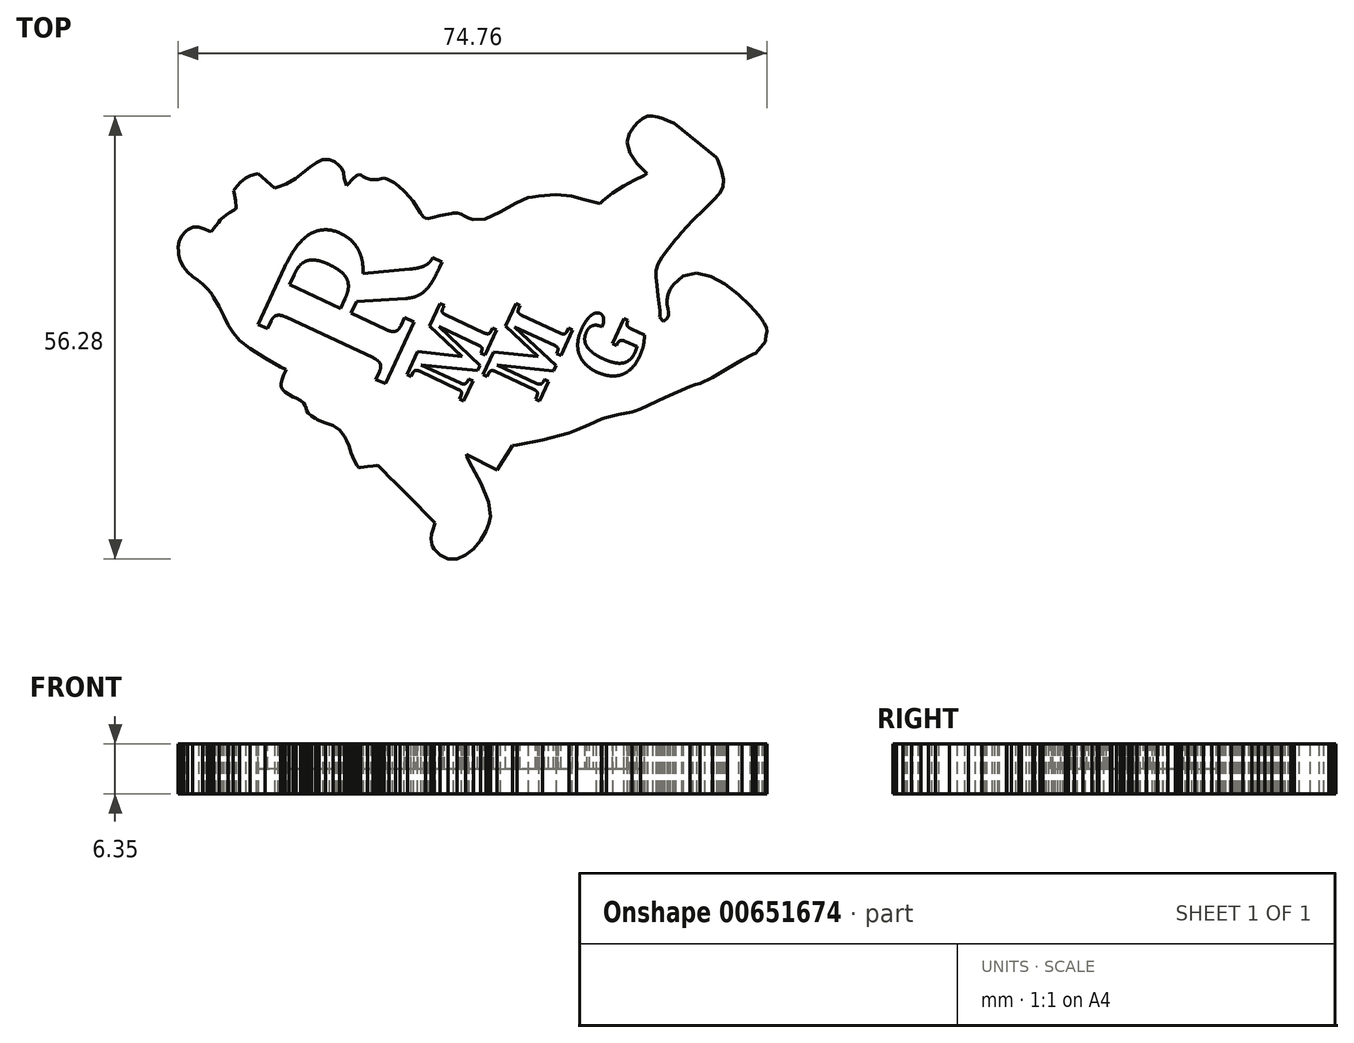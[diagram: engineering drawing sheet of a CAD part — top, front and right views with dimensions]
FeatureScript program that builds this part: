
annotation { "Feature Type Name" : "Feature", "Feature Type Description" : "" }
export const myFeature = defineFeature(function(context is Context, id is Id, definition is map)
    precondition{}
    {
        {
            var Q0;
            Q0=qCreatedBy(makeId("Top.planeOp"),FACE);
            var sketch = newSketch(context, id + "F0", { "sketchPlane" : qUnion([Q0])});
            skLineSegment(sketch, "E0", {"start": v(36, -1.99) * mm, "end": v(37.2, -0.53) * mm});
            skLineSegment(sketch, "E1", {"start": v(37.2, -0.53) * mm, "end": v(37.2, -0.33) * mm});
            skLineSegment(sketch, "E2", {"start": v(37.2, -0.33) * mm, "end": v(37.29, 0.26) * mm});
            skLineSegment(sketch, "E3", {"start": v(37.29, 0.26) * mm, "end": v(37.38, 0.75) * mm});
            skLineSegment(sketch, "E4", {"start": v(37.38, 0.75) * mm, "end": v(37.3, 1.24) * mm});
            skLineSegment(sketch, "E5", {"start": v(37.3, 1.24) * mm, "end": v(37, 1.85) * mm});
            skLineSegment(sketch, "E6", {"start": v(37, 1.85) * mm, "end": v(36.9, 2.04) * mm});
            skLineSegment(sketch, "E7", {"start": v(36.9, 2.04) * mm, "end": v(36.76, 2.25) * mm});
            skLineSegment(sketch, "E8", {"start": v(36.76, 2.25) * mm, "end": v(36.3, 2.84) * mm});
            skLineSegment(sketch, "E9", {"start": v(36.3, 2.84) * mm, "end": v(35.23, 4.06) * mm});
            skLineSegment(sketch, "E10", {"start": v(35.23, 4.06) * mm, "end": v(33.79, 5.46) * mm});
            skLineSegment(sketch, "E11", {"start": v(33.79, 5.46) * mm, "end": v(32.1, 6.77) * mm});
            skLineSegment(sketch, "E12", {"start": v(32.1, 6.77) * mm, "end": v(30.27, 7.76) * mm});
            skLineSegment(sketch, "E13", {"start": v(30.27, 7.76) * mm, "end": v(28.44, 8.18) * mm});
            skLineSegment(sketch, "E14", {"start": v(28.44, 8.18) * mm, "end": v(26.72, 7.78) * mm});
            skLineSegment(sketch, "E15", {"start": v(26.72, 7.78) * mm, "end": v(25.5, 6.74) * mm});
            skLineSegment(sketch, "E16", {"start": v(25.5, 6.74) * mm, "end": v(25.23, 6.3) * mm});
            skLineSegment(sketch, "E17", {"start": v(25.23, 6.3) * mm, "end": v(25.1, 6.12) * mm});
            skLineSegment(sketch, "E18", {"start": v(25.1, 6.12) * mm, "end": v(24.82, 5.48) * mm});
            skLineSegment(sketch, "E19", {"start": v(24.82, 5.48) * mm, "end": v(24.68, 4.78) * mm});
            skLineSegment(sketch, "E20", {"start": v(24.68, 4.78) * mm, "end": v(24.7, 4.17) * mm});
            skLineSegment(sketch, "E21", {"start": v(24.7, 4.17) * mm, "end": v(24.8, 3.65) * mm});
            skLineSegment(sketch, "E22", {"start": v(24.8, 3.65) * mm, "end": v(24.9, 3.2) * mm});
            skLineSegment(sketch, "E23", {"start": v(24.9, 3.2) * mm, "end": v(24.9, 2.8) * mm});
            skLineSegment(sketch, "E24", {"start": v(24.9, 2.8) * mm, "end": v(24.7, 2.42) * mm});
            skLineSegment(sketch, "E25", {"start": v(24.7, 2.42) * mm, "end": v(24.35, 2.14) * mm});
            skLineSegment(sketch, "E26", {"start": v(24.35, 2.14) * mm, "end": v(24.22, 2.07) * mm});
            skLineSegment(sketch, "E27", {"start": v(24.22, 2.07) * mm, "end": v(24.13, 2.18) * mm});
            skLineSegment(sketch, "E28", {"start": v(24.13, 2.18) * mm, "end": v(23.84, 2.5) * mm});
            skLineSegment(sketch, "E29", {"start": v(23.84, 2.5) * mm, "end": v(23.75, 2.6) * mm});
            skLineSegment(sketch, "E30", {"start": v(23.75, 2.6) * mm, "end": v(23.8, 2.8) * mm});
            skLineSegment(sketch, "E31", {"start": v(23.8, 2.8) * mm, "end": v(23.8, 3.28) * mm});
            skLineSegment(sketch, "E32", {"start": v(23.8, 3.28) * mm, "end": v(23.8, 3.44) * mm});
            skLineSegment(sketch, "E33", {"start": v(23.8, 3.44) * mm, "end": v(23.75, 3.9) * mm});
            skLineSegment(sketch, "E34", {"start": v(23.75, 3.9) * mm, "end": v(23.58, 5.26) * mm});
            skLineSegment(sketch, "E35", {"start": v(23.58, 5.26) * mm, "end": v(23.4, 6.62) * mm});
            skLineSegment(sketch, "E36", {"start": v(23.4, 6.62) * mm, "end": v(23.28, 7.67) * mm});
            skLineSegment(sketch, "E37", {"start": v(23.28, 7.67) * mm, "end": v(23.31, 8.52) * mm});
            skLineSegment(sketch, "E38", {"start": v(23.31, 8.52) * mm, "end": v(23.55, 9.33) * mm});
            skLineSegment(sketch, "E39", {"start": v(23.55, 9.33) * mm, "end": v(24.04, 10.22) * mm});
            skLineSegment(sketch, "E40", {"start": v(24.04, 10.22) * mm, "end": v(24.86, 11.32) * mm});
            skLineSegment(sketch, "E41", {"start": v(24.86, 11.32) * mm, "end": v(25.77, 12.41) * mm});
            skLineSegment(sketch, "E42", {"start": v(25.77, 12.41) * mm, "end": v(26.07, 12.77) * mm});
            skLineSegment(sketch, "E43", {"start": v(26.07, 12.77) * mm, "end": v(26.53, 13.3) * mm});
            skLineSegment(sketch, "E44", {"start": v(26.53, 13.3) * mm, "end": v(27.95, 14.84) * mm});
            skLineSegment(sketch, "E45", {"start": v(27.95, 14.84) * mm, "end": v(29.45, 16.34) * mm});
            skLineSegment(sketch, "E46", {"start": v(29.45, 16.34) * mm, "end": v(30.6, 17.44) * mm});
            skLineSegment(sketch, "E47", {"start": v(30.6, 17.44) * mm, "end": v(31.39, 18.31) * mm});
            skLineSegment(sketch, "E48", {"start": v(31.39, 18.31) * mm, "end": v(31.82, 19.12) * mm});
            skLineSegment(sketch, "E49", {"start": v(31.82, 19.12) * mm, "end": v(31.9, 20.03) * mm});
            skLineSegment(sketch, "E50", {"start": v(31.9, 20.03) * mm, "end": v(31.62, 21.22) * mm});
            skLineSegment(sketch, "E51", {"start": v(31.62, 21.22) * mm, "end": v(31.16, 22.44) * mm});
            skLineSegment(sketch, "E52", {"start": v(31.16, 22.44) * mm, "end": v(30.99, 22.84) * mm});
            skLineSegment(sketch, "E53", {"start": v(30.99, 22.84) * mm, "end": v(25.6, 27.24) * mm});
            skLineSegment(sketch, "E54", {"start": v(25.6, 27.24) * mm, "end": v(25.42, 27.3) * mm});
            skLineSegment(sketch, "E55", {"start": v(25.42, 27.3) * mm, "end": v(24.88, 27.5) * mm});
            skLineSegment(sketch, "E56", {"start": v(24.88, 27.5) * mm, "end": v(24.2, 27.79) * mm});
            skLineSegment(sketch, "E57", {"start": v(24.2, 27.79) * mm, "end": v(23.53, 28.02) * mm});
            skLineSegment(sketch, "E58", {"start": v(23.53, 28.02) * mm, "end": v(22.88, 28.14) * mm});
            skLineSegment(sketch, "E59", {"start": v(22.88, 28.14) * mm, "end": v(22.23, 28.1) * mm});
            skLineSegment(sketch, "E60", {"start": v(22.23, 28.1) * mm, "end": v(21.57, 27.81) * mm});
            skLineSegment(sketch, "E61", {"start": v(21.57, 27.81) * mm, "end": v(20.89, 27.24) * mm});
            skLineSegment(sketch, "E62", {"start": v(20.89, 27.24) * mm, "end": v(20.33, 26.55) * mm});
            skLineSegment(sketch, "E63", {"start": v(20.33, 26.55) * mm, "end": v(20.17, 26.3) * mm});
            skLineSegment(sketch, "E64", {"start": v(20.17, 26.3) * mm, "end": v(19.96, 25.98) * mm});
            skLineSegment(sketch, "E65", {"start": v(19.96, 25.98) * mm, "end": v(19.65, 24.8) * mm});
            skLineSegment(sketch, "E66", {"start": v(19.65, 24.8) * mm, "end": v(19.97, 23.43) * mm});
            skLineSegment(sketch, "E67", {"start": v(19.97, 23.43) * mm, "end": v(20.89, 22.11) * mm});
            skLineSegment(sketch, "E68", {"start": v(20.89, 22.11) * mm, "end": v(21.84, 21.12) * mm});
            skLineSegment(sketch, "E69", {"start": v(21.84, 21.12) * mm, "end": v(22.18, 20.8) * mm});
            skLineSegment(sketch, "E70", {"start": v(22.18, 20.8) * mm, "end": v(21.78, 20.59) * mm});
            skLineSegment(sketch, "E71", {"start": v(21.78, 20.59) * mm, "end": v(20.56, 19.98) * mm});
            skLineSegment(sketch, "E72", {"start": v(20.56, 19.98) * mm, "end": v(19.14, 19.26) * mm});
            skLineSegment(sketch, "E73", {"start": v(19.14, 19.26) * mm, "end": v(17.75, 18.35) * mm});
            skLineSegment(sketch, "E74", {"start": v(17.75, 18.35) * mm, "end": v(16.58, 17.37) * mm});
            skLineSegment(sketch, "E75", {"start": v(16.58, 17.37) * mm, "end": v(16.22, 17.02) * mm});
            skLineSegment(sketch, "E76", {"start": v(16.22, 17.02) * mm, "end": v(15.7, 17.11) * mm});
            skLineSegment(sketch, "E77", {"start": v(15.7, 17.11) * mm, "end": v(14.18, 17.51) * mm});
            skLineSegment(sketch, "E78", {"start": v(14.18, 17.51) * mm, "end": v(12.57, 17.95) * mm});
            skLineSegment(sketch, "E79", {"start": v(12.57, 17.95) * mm, "end": v(10.63, 18.13) * mm});
            skLineSegment(sketch, "E80", {"start": v(10.63, 18.13) * mm, "end": v(8.36, 17.97) * mm});
            skLineSegment(sketch, "E81", {"start": v(8.36, 17.97) * mm, "end": v(7.62, 17.86) * mm});
            skLineSegment(sketch, "E82", {"start": v(7.62, 17.86) * mm, "end": v(7.07, 17.77) * mm});
            skLineSegment(sketch, "E83", {"start": v(7.07, 17.77) * mm, "end": v(5.49, 17.1) * mm});
            skLineSegment(sketch, "E84", {"start": v(5.49, 17.1) * mm, "end": v(3.52, 15.94) * mm});
            skLineSegment(sketch, "E85", {"start": v(3.52, 15.94) * mm, "end": v(1.6, 15.06) * mm});
            skLineSegment(sketch, "E86", {"start": v(1.6, 15.06) * mm, "end": v(0.08, 14.95) * mm});
            skLineSegment(sketch, "E87", {"start": v(0.08, 14.95) * mm, "end": v(-0.35, 15.1) * mm});
            skLineSegment(sketch, "E88", {"start": v(-0.35, 15.1) * mm, "end": v(-0.53, 15.17) * mm});
            skLineSegment(sketch, "E89", {"start": v(-0.53, 15.17) * mm, "end": v(-1.03, 15.43) * mm});
            skLineSegment(sketch, "E90", {"start": v(-1.03, 15.43) * mm, "end": v(-1.44, 15.68) * mm});
            skLineSegment(sketch, "E91", {"start": v(-1.44, 15.68) * mm, "end": v(-1.9, 15.81) * mm});
            skLineSegment(sketch, "E92", {"start": v(-1.9, 15.81) * mm, "end": v(-2.48, 15.78) * mm});
            skLineSegment(sketch, "E93", {"start": v(-2.48, 15.78) * mm, "end": v(-2.67, 15.75) * mm});
            skLineSegment(sketch, "E94", {"start": v(-2.67, 15.75) * mm, "end": v(-3.03, 15.68) * mm});
            skLineSegment(sketch, "E95", {"start": v(-3.03, 15.68) * mm, "end": v(-4.11, 15.47) * mm});
            skLineSegment(sketch, "E96", {"start": v(-4.11, 15.47) * mm, "end": v(-5.07, 15.25) * mm});
            skLineSegment(sketch, "E97", {"start": v(-5.07, 15.25) * mm, "end": v(-5.67, 15.14) * mm});
            skLineSegment(sketch, "E98", {"start": v(-5.67, 15.14) * mm, "end": v(-6.05, 15.17) * mm});
            skLineSegment(sketch, "E99", {"start": v(-6.05, 15.17) * mm, "end": v(-6.32, 15.38) * mm});
            skLineSegment(sketch, "E100", {"start": v(-6.32, 15.38) * mm, "end": v(-6.61, 15.82) * mm});
            skLineSegment(sketch, "E101", {"start": v(-6.61, 15.82) * mm, "end": v(-7.05, 16.53) * mm});
            skLineSegment(sketch, "E102", {"start": v(-7.05, 16.53) * mm, "end": v(-7.56, 17.3) * mm});
            skLineSegment(sketch, "E103", {"start": v(-7.56, 17.3) * mm, "end": v(-7.75, 17.54) * mm});
            skLineSegment(sketch, "E104", {"start": v(-7.75, 17.54) * mm, "end": v(-7.87, 17.7) * mm});
            skLineSegment(sketch, "E105", {"start": v(-7.87, 17.7) * mm, "end": v(-8.74, 18.65) * mm});
            skLineSegment(sketch, "E106", {"start": v(-8.74, 18.65) * mm, "end": v(-9.8, 19.52) * mm});
            skLineSegment(sketch, "E107", {"start": v(-9.8, 19.52) * mm, "end": v(-10, 19.65) * mm});
            skLineSegment(sketch, "E108", {"start": v(-10, 19.65) * mm, "end": v(-10.2, 19.78) * mm});
            skLineSegment(sketch, "E109", {"start": v(-10.2, 19.78) * mm, "end": v(-10.84, 20.13) * mm});
            skLineSegment(sketch, "E110", {"start": v(-10.84, 20.13) * mm, "end": v(-11.25, 20.24) * mm});
            skLineSegment(sketch, "E111", {"start": v(-11.25, 20.24) * mm, "end": v(-11.57, 20.16) * mm});
            skLineSegment(sketch, "E112", {"start": v(-11.57, 20.16) * mm, "end": v(-11.98, 20.06) * mm});
            skLineSegment(sketch, "E113", {"start": v(-11.98, 20.06) * mm, "end": v(-12.12, 20.05) * mm});
            skLineSegment(sketch, "E114", {"start": v(-12.12, 20.05) * mm, "end": v(-12.33, 20.04) * mm});
            skLineSegment(sketch, "E115", {"start": v(-12.33, 20.04) * mm, "end": v(-12.96, 20.07) * mm});
            skLineSegment(sketch, "E116", {"start": v(-12.96, 20.07) * mm, "end": v(-13.51, 20.24) * mm});
            skLineSegment(sketch, "E117", {"start": v(-13.51, 20.24) * mm, "end": v(-13.88, 20.47) * mm});
            skLineSegment(sketch, "E118", {"start": v(-13.88, 20.47) * mm, "end": v(-14.15, 20.66) * mm});
            skLineSegment(sketch, "E119", {"start": v(-14.15, 20.66) * mm, "end": v(-14.41, 20.72) * mm});
            skLineSegment(sketch, "E120", {"start": v(-14.41, 20.72) * mm, "end": v(-14.74, 20.58) * mm});
            skLineSegment(sketch, "E121", {"start": v(-14.74, 20.58) * mm, "end": v(-15.24, 20.13) * mm});
            skLineSegment(sketch, "E122", {"start": v(-15.24, 20.13) * mm, "end": v(-15.8, 19.5) * mm});
            skLineSegment(sketch, "E123", {"start": v(-15.8, 19.5) * mm, "end": v(-15.99, 19.29) * mm});
            skLineSegment(sketch, "E124", {"start": v(-15.99, 19.29) * mm, "end": v(-16.1, 19.5) * mm});
            skLineSegment(sketch, "E125", {"start": v(-16.1, 19.5) * mm, "end": v(-16.3, 20.22) * mm});
            skLineSegment(sketch, "E126", {"start": v(-16.3, 20.22) * mm, "end": v(-16.4, 20.93) * mm});
            skLineSegment(sketch, "E127", {"start": v(-16.4, 20.93) * mm, "end": v(-16.64, 21.53) * mm});
            skLineSegment(sketch, "E128", {"start": v(-16.64, 21.53) * mm, "end": v(-17.15, 22.05) * mm});
            skLineSegment(sketch, "E129", {"start": v(-17.15, 22.05) * mm, "end": v(-17.34, 22.18) * mm});
            skLineSegment(sketch, "E130", {"start": v(-17.34, 22.18) * mm, "end": v(-17.55, 22.32) * mm});
            skLineSegment(sketch, "E131", {"start": v(-17.55, 22.32) * mm, "end": v(-18.25, 22.6) * mm});
            skLineSegment(sketch, "E132", {"start": v(-18.25, 22.6) * mm, "end": v(-19.07, 22.57) * mm});
            skLineSegment(sketch, "E133", {"start": v(-19.07, 22.57) * mm, "end": v(-19.85, 22.22) * mm});
            skLineSegment(sketch, "E134", {"start": v(-19.85, 22.22) * mm, "end": v(-20.64, 21.63) * mm});
            skLineSegment(sketch, "E135", {"start": v(-20.64, 21.63) * mm, "end": v(-21.5, 20.92) * mm});
            skLineSegment(sketch, "E136", {"start": v(-21.5, 20.92) * mm, "end": v(-22.5, 20.17) * mm});
            skLineSegment(sketch, "E137", {"start": v(-22.5, 20.17) * mm, "end": v(-23.7, 19.5) * mm});
            skLineSegment(sketch, "E138", {"start": v(-23.7, 19.5) * mm, "end": v(-24.78, 19.1) * mm});
            skLineSegment(sketch, "E139", {"start": v(-24.78, 19.1) * mm, "end": v(-25.15, 19) * mm});
            skLineSegment(sketch, "E140", {"start": v(-25.15, 19) * mm, "end": v(-27.25, 20.81) * mm});
            skLineSegment(sketch, "E141", {"start": v(-27.25, 20.81) * mm, "end": v(-27.48, 20.75) * mm});
            skLineSegment(sketch, "E142", {"start": v(-27.48, 20.75) * mm, "end": v(-28.18, 20.56) * mm});
            skLineSegment(sketch, "E143", {"start": v(-28.18, 20.56) * mm, "end": v(-28.85, 20.24) * mm});
            skLineSegment(sketch, "E144", {"start": v(-28.85, 20.24) * mm, "end": v(-29.5, 19.67) * mm});
            skLineSegment(sketch, "E145", {"start": v(-29.5, 19.67) * mm, "end": v(-30.17, 18.9) * mm});
            skLineSegment(sketch, "E146", {"start": v(-30.17, 18.9) * mm, "end": v(-30.38, 18.64) * mm});
            skLineSegment(sketch, "E147", {"start": v(-30.38, 18.64) * mm, "end": v(-30.32, 18.41) * mm});
            skLineSegment(sketch, "E148", {"start": v(-30.32, 18.41) * mm, "end": v(-30.1, 17.38) * mm});
            skLineSegment(sketch, "E149", {"start": v(-30.1, 17.38) * mm, "end": v(-30.06, 16.48) * mm});
            skLineSegment(sketch, "E150", {"start": v(-30.06, 16.48) * mm, "end": v(-30.09, 16.33) * mm});
            skLineSegment(sketch, "E151", {"start": v(-30.09, 16.33) * mm, "end": v(-30.27, 16.21) * mm});
            skLineSegment(sketch, "E152", {"start": v(-30.27, 16.21) * mm, "end": v(-30.83, 15.86) * mm});
            skLineSegment(sketch, "E153", {"start": v(-30.83, 15.86) * mm, "end": v(-31.33, 15.55) * mm});
            skLineSegment(sketch, "E154", {"start": v(-31.33, 15.55) * mm, "end": v(-31.64, 15.32) * mm});
            skLineSegment(sketch, "E155", {"start": v(-31.64, 15.32) * mm, "end": v(-31.85, 15.13) * mm});
            skLineSegment(sketch, "E156", {"start": v(-31.85, 15.13) * mm, "end": v(-32.04, 14.9) * mm});
            skLineSegment(sketch, "E157", {"start": v(-32.04, 14.9) * mm, "end": v(-32.28, 14.59) * mm});
            skLineSegment(sketch, "E158", {"start": v(-32.28, 14.59) * mm, "end": v(-32.66, 14.12) * mm});
            skLineSegment(sketch, "E159", {"start": v(-32.66, 14.12) * mm, "end": v(-33.09, 13.61) * mm});
            skLineSegment(sketch, "E160", {"start": v(-33.09, 13.61) * mm, "end": v(-33.23, 13.44) * mm});
            skLineSegment(sketch, "E161", {"start": v(-33.23, 13.44) * mm, "end": v(-33.45, 13.52) * mm});
            skLineSegment(sketch, "E162", {"start": v(-33.45, 13.52) * mm, "end": v(-34.07, 13.78) * mm});
            skLineSegment(sketch, "E163", {"start": v(-34.07, 13.78) * mm, "end": v(-34.79, 14.03) * mm});
            skLineSegment(sketch, "E164", {"start": v(-34.79, 14.03) * mm, "end": v(-35.5, 14.03) * mm});
            skLineSegment(sketch, "E165", {"start": v(-35.5, 14.03) * mm, "end": v(-36.13, 13.73) * mm});
            skLineSegment(sketch, "E166", {"start": v(-36.13, 13.73) * mm, "end": v(-36.3, 13.58) * mm});
            skLineSegment(sketch, "E167", {"start": v(-36.3, 13.58) * mm, "end": v(-36.49, 13.44) * mm});
            skLineSegment(sketch, "E168", {"start": v(-36.49, 13.44) * mm, "end": v(-36.94, 12.91) * mm});
            skLineSegment(sketch, "E169", {"start": v(-36.94, 12.91) * mm, "end": v(-37.27, 12.19) * mm});
            skLineSegment(sketch, "E170", {"start": v(-37.27, 12.19) * mm, "end": v(-37.38, 11.46) * mm});
            skLineSegment(sketch, "E171", {"start": v(-37.38, 11.46) * mm, "end": v(-37.37, 10.94) * mm});
            skLineSegment(sketch, "E172", {"start": v(-37.37, 10.94) * mm, "end": v(-37.35, 10.77) * mm});
            skLineSegment(sketch, "E173", {"start": v(-37.35, 10.77) * mm, "end": v(-37.32, 10.52) * mm});
            skLineSegment(sketch, "E174", {"start": v(-37.32, 10.52) * mm, "end": v(-37.13, 9.76) * mm});
            skLineSegment(sketch, "E175", {"start": v(-37.13, 9.76) * mm, "end": v(-36.73, 8.96) * mm});
            skLineSegment(sketch, "E176", {"start": v(-36.73, 8.96) * mm, "end": v(-36.21, 8.31) * mm});
            skLineSegment(sketch, "E177", {"start": v(-36.21, 8.31) * mm, "end": v(-35.6, 7.77) * mm});
            skLineSegment(sketch, "E178", {"start": v(-35.6, 7.77) * mm, "end": v(-34.94, 7.27) * mm});
            skLineSegment(sketch, "E179", {"start": v(-34.94, 7.27) * mm, "end": v(-34.28, 6.76) * mm});
            skLineSegment(sketch, "E180", {"start": v(-34.28, 6.76) * mm, "end": v(-33.65, 6.18) * mm});
            skLineSegment(sketch, "E181", {"start": v(-33.65, 6.18) * mm, "end": v(-33.23, 5.67) * mm});
            skLineSegment(sketch, "E182", {"start": v(-33.23, 5.67) * mm, "end": v(-33.1, 5.48) * mm});
            skLineSegment(sketch, "E183", {"start": v(-33.1, 5.48) * mm, "end": v(-32.87, 5.1) * mm});
            skLineSegment(sketch, "E184", {"start": v(-32.87, 5.1) * mm, "end": v(-32.22, 3.93) * mm});
            skLineSegment(sketch, "E185", {"start": v(-32.22, 3.93) * mm, "end": v(-31.6, 2.66) * mm});
            skLineSegment(sketch, "E186", {"start": v(-31.6, 2.66) * mm, "end": v(-31.06, 1.58) * mm});
            skLineSegment(sketch, "E187", {"start": v(-31.06, 1.58) * mm, "end": v(-30.44, 0.6) * mm});
            skLineSegment(sketch, "E188", {"start": v(-30.44, 0.6) * mm, "end": v(-29.57, -0.36) * mm});
            skLineSegment(sketch, "E189", {"start": v(-29.57, -0.36) * mm, "end": v(-28.27, -1.4) * mm});
            skLineSegment(sketch, "E190", {"start": v(-28.27, -1.4) * mm, "end": v(-26.37, -2.62) * mm});
            skLineSegment(sketch, "E191", {"start": v(-26.37, -2.62) * mm, "end": v(-24.37, -3.74) * mm});
            skLineSegment(sketch, "E192", {"start": v(-24.37, -3.74) * mm, "end": v(-23.7, -4.1) * mm});
            skLineSegment(sketch, "E193", {"start": v(-23.7, -4.1) * mm, "end": v(-23.77, -4.27) * mm});
            skLineSegment(sketch, "E194", {"start": v(-23.77, -4.27) * mm, "end": v(-23.99, -4.78) * mm});
            skLineSegment(sketch, "E195", {"start": v(-23.99, -4.78) * mm, "end": v(-24.2, -5.35) * mm});
            skLineSegment(sketch, "E196", {"start": v(-24.2, -5.35) * mm, "end": v(-24.32, -5.82) * mm});
            skLineSegment(sketch, "E197", {"start": v(-24.32, -5.82) * mm, "end": v(-24.32, -6.23) * mm});
            skLineSegment(sketch, "E198", {"start": v(-24.32, -6.23) * mm, "end": v(-24.16, -6.58) * mm});
            skLineSegment(sketch, "E199", {"start": v(-24.16, -6.58) * mm, "end": v(-23.84, -6.92) * mm});
            skLineSegment(sketch, "E200", {"start": v(-23.84, -6.92) * mm, "end": v(-23.33, -7.26) * mm});
            skLineSegment(sketch, "E201", {"start": v(-23.33, -7.26) * mm, "end": v(-22.78, -7.54) * mm});
            skLineSegment(sketch, "E202", {"start": v(-22.78, -7.54) * mm, "end": v(-22.6, -7.62) * mm});
            skLineSegment(sketch, "E203", {"start": v(-22.6, -7.62) * mm, "end": v(-22.41, -7.7) * mm});
            skLineSegment(sketch, "E204", {"start": v(-22.41, -7.7) * mm, "end": v(-21.87, -8) * mm});
            skLineSegment(sketch, "E205", {"start": v(-21.87, -8) * mm, "end": v(-21.46, -8.35) * mm});
            skLineSegment(sketch, "E206", {"start": v(-21.46, -8.35) * mm, "end": v(-21.25, -8.66) * mm});
            skLineSegment(sketch, "E207", {"start": v(-21.25, -8.66) * mm, "end": v(-21.16, -8.97) * mm});
            skLineSegment(sketch, "E208", {"start": v(-21.16, -8.97) * mm, "end": v(-21.06, -9.27) * mm});
            skLineSegment(sketch, "E209", {"start": v(-21.06, -9.27) * mm, "end": v(-20.87, -9.6) * mm});
            skLineSegment(sketch, "E210", {"start": v(-20.87, -9.6) * mm, "end": v(-20.48, -9.98) * mm});
            skLineSegment(sketch, "E211", {"start": v(-20.48, -9.98) * mm, "end": v(-19.96, -10.3) * mm});
            skLineSegment(sketch, "E212", {"start": v(-19.96, -10.3) * mm, "end": v(-19.78, -10.4) * mm});
            skLineSegment(sketch, "E213", {"start": v(-19.78, -10.4) * mm, "end": v(-19.52, -10.54) * mm});
            skLineSegment(sketch, "E214", {"start": v(-19.52, -10.54) * mm, "end": v(-18.68, -10.86) * mm});
            skLineSegment(sketch, "E215", {"start": v(-18.68, -10.86) * mm, "end": v(-17.73, -11.21) * mm});
            skLineSegment(sketch, "E216", {"start": v(-17.73, -11.21) * mm, "end": v(-16.88, -11.77) * mm});
            skLineSegment(sketch, "E217", {"start": v(-16.88, -11.77) * mm, "end": v(-16.26, -12.56) * mm});
            skLineSegment(sketch, "E218", {"start": v(-16.26, -12.56) * mm, "end": v(-16.1, -12.86) * mm});
            skLineSegment(sketch, "E219", {"start": v(-16.1, -12.86) * mm, "end": v(-15.99, -13.08) * mm});
            skLineSegment(sketch, "E220", {"start": v(-15.99, -13.08) * mm, "end": v(-15.7, -13.8) * mm});
            skLineSegment(sketch, "E221", {"start": v(-15.7, -13.8) * mm, "end": v(-15.42, -14.67) * mm});
            skLineSegment(sketch, "E222", {"start": v(-15.42, -14.67) * mm, "end": v(-15.07, -15.54) * mm});
            skLineSegment(sketch, "E223", {"start": v(-15.07, -15.54) * mm, "end": v(-14.65, -16.28) * mm});
            skLineSegment(sketch, "E224", {"start": v(-14.65, -16.28) * mm, "end": v(-14.49, -16.51) * mm});
            skLineSegment(sketch, "E225", {"start": v(-14.49, -16.51) * mm, "end": v(-14.2, -16.5) * mm});
            skLineSegment(sketch, "E226", {"start": v(-14.2, -16.5) * mm, "end": v(-13.36, -16.42) * mm});
            skLineSegment(sketch, "E227", {"start": v(-13.36, -16.42) * mm, "end": v(-12.65, -16.32) * mm});
            skLineSegment(sketch, "E228", {"start": v(-12.65, -16.32) * mm, "end": v(-12.22, -16.28) * mm});
            skLineSegment(sketch, "E229", {"start": v(-12.22, -16.28) * mm, "end": v(-11.94, -16.34) * mm});
            skLineSegment(sketch, "E230", {"start": v(-11.94, -16.34) * mm, "end": v(-11.66, -16.56) * mm});
            skLineSegment(sketch, "E231", {"start": v(-11.66, -16.56) * mm, "end": v(-11.26, -17) * mm});
            skLineSegment(sketch, "E232", {"start": v(-11.26, -17) * mm, "end": v(-10.6, -17.72) * mm});
            skLineSegment(sketch, "E233", {"start": v(-10.6, -17.72) * mm, "end": v(-9.8, -18.51) * mm});
            skLineSegment(sketch, "E234", {"start": v(-9.8, -18.51) * mm, "end": v(-9.52, -18.77) * mm});
            skLineSegment(sketch, "E235", {"start": v(-9.52, -18.77) * mm, "end": v(-9.2, -19.07) * mm});
            skLineSegment(sketch, "E236", {"start": v(-9.2, -19.07) * mm, "end": v(-8.25, -20) * mm});
            skLineSegment(sketch, "E237", {"start": v(-8.25, -20) * mm, "end": v(-7.1, -21.18) * mm});
            skLineSegment(sketch, "E238", {"start": v(-7.1, -21.18) * mm, "end": v(-5.98, -22.34) * mm});
            skLineSegment(sketch, "E239", {"start": v(-5.98, -22.34) * mm, "end": v(-5.07, -23.25) * mm});
            skLineSegment(sketch, "E240", {"start": v(-5.07, -23.25) * mm, "end": v(-4.76, -23.55) * mm});
            skLineSegment(sketch, "E241", {"start": v(-4.76, -23.55) * mm, "end": v(-4.8, -23.76) * mm});
            skLineSegment(sketch, "E242", {"start": v(-4.8, -23.76) * mm, "end": v(-5, -24.36) * mm});
            skLineSegment(sketch, "E243", {"start": v(-5, -24.36) * mm, "end": v(-5.2, -24.98) * mm});
            skLineSegment(sketch, "E244", {"start": v(-5.2, -24.98) * mm, "end": v(-5.26, -25.63) * mm});
            skLineSegment(sketch, "E245", {"start": v(-5.26, -25.63) * mm, "end": v(-5.16, -26.33) * mm});
            skLineSegment(sketch, "E246", {"start": v(-5.16, -26.33) * mm, "end": v(-5.1, -26.55) * mm});
            skLineSegment(sketch, "E247", {"start": v(-5.1, -26.55) * mm, "end": v(-4.92, -26.86) * mm});
            skLineSegment(sketch, "E248", {"start": v(-4.92, -26.86) * mm, "end": v(-4.15, -27.65) * mm});
            skLineSegment(sketch, "E249", {"start": v(-4.15, -27.65) * mm, "end": v(-3.1, -28.14) * mm});
            skLineSegment(sketch, "E250", {"start": v(-3.1, -28.14) * mm, "end": v(-1.99, -28.11) * mm});
            skLineSegment(sketch, "E251", {"start": v(-1.99, -28.11) * mm, "end": v(-0.9, -27.65) * mm});
            skLineSegment(sketch, "E252", {"start": v(-0.9, -27.65) * mm, "end": v(0.13, -26.85) * mm});
            skLineSegment(sketch, "E253", {"start": v(0.13, -26.85) * mm, "end": v(1.02, -25.8) * mm});
            skLineSegment(sketch, "E254", {"start": v(1.02, -25.8) * mm, "end": v(1.71, -24.57) * mm});
            skLineSegment(sketch, "E255", {"start": v(1.71, -24.57) * mm, "end": v(2.08, -23.6) * mm});
            skLineSegment(sketch, "E256", {"start": v(2.08, -23.6) * mm, "end": v(2.16, -23.26) * mm});
            skLineSegment(sketch, "E257", {"start": v(2.16, -23.26) * mm, "end": v(2.28, -22.72) * mm});
            skLineSegment(sketch, "E258", {"start": v(2.28, -22.72) * mm, "end": v(2.03, -20.93) * mm});
            skLineSegment(sketch, "E259", {"start": v(2.03, -20.93) * mm, "end": v(1.07, -18.56) * mm});
            skLineSegment(sketch, "E260", {"start": v(1.07, -18.56) * mm, "end": v(-0.07, -16.43) * mm});
            skLineSegment(sketch, "E261", {"start": v(-0.07, -16.43) * mm, "end": v(-0.68, -15.26) * mm});
            skLineSegment(sketch, "E262", {"start": v(-0.68, -15.26) * mm, "end": v(-0.76, -14.85) * mm});
            skLineSegment(sketch, "E263", {"start": v(-0.76, -14.85) * mm, "end": v(3.1, -16.84) * mm});
            skLineSegment(sketch, "E264", {"start": v(3.1, -16.84) * mm, "end": v(5.05, -13.71) * mm});
            skLineSegment(sketch, "E265", {"start": v(5.05, -13.71) * mm, "end": v(5.62, -13.66) * mm});
            skLineSegment(sketch, "E266", {"start": v(5.62, -13.66) * mm, "end": v(8.9, -13.05) * mm});
            skLineSegment(sketch, "E267", {"start": v(8.9, -13.05) * mm, "end": v(12.27, -12.12) * mm});
            skLineSegment(sketch, "E268", {"start": v(12.27, -12.12) * mm, "end": v(12.88, -11.9) * mm});
            skLineSegment(sketch, "E269", {"start": v(12.88, -11.9) * mm, "end": v(13.23, -11.79) * mm});
            skLineSegment(sketch, "E270", {"start": v(13.23, -11.79) * mm, "end": v(14.83, -11.08) * mm});
            skLineSegment(sketch, "E271", {"start": v(14.83, -11.08) * mm, "end": v(16.4, -10.37) * mm});
            skLineSegment(sketch, "E272", {"start": v(16.4, -10.37) * mm, "end": v(16.73, -10.24) * mm});
            skLineSegment(sketch, "E273", {"start": v(16.73, -10.24) * mm, "end": v(17.01, -10.14) * mm});
            skLineSegment(sketch, "E274", {"start": v(17.01, -10.14) * mm, "end": v(18.54, -9.81) * mm});
            skLineSegment(sketch, "E275", {"start": v(18.54, -9.81) * mm, "end": v(20.26, -9.44) * mm});
            skLineSegment(sketch, "E276", {"start": v(20.26, -9.44) * mm, "end": v(20.63, -9.31) * mm});
            skLineSegment(sketch, "E277", {"start": v(20.63, -9.31) * mm, "end": v(21.3, -9.08) * mm});
            skLineSegment(sketch, "E278", {"start": v(21.3, -9.08) * mm, "end": v(24.47, -7.65) * mm});
            skLineSegment(sketch, "E279", {"start": v(24.47, -7.65) * mm, "end": v(27.64, -6.23) * mm});
            skLineSegment(sketch, "E280", {"start": v(27.64, -6.23) * mm, "end": v(28.3, -6) * mm});
            skLineSegment(sketch, "E281", {"start": v(28.3, -6) * mm, "end": v(28.86, -5.82) * mm});
            skLineSegment(sketch, "E282", {"start": v(28.86, -5.82) * mm, "end": v(30.46, -5.08) * mm});
            skLineSegment(sketch, "E283", {"start": v(30.46, -5.08) * mm, "end": v(32.4, -3.97) * mm});
            skLineSegment(sketch, "E284", {"start": v(32.4, -3.97) * mm, "end": v(34.2, -2.87) * mm});
            skLineSegment(sketch, "E285", {"start": v(34.2, -2.87) * mm, "end": v(35.54, -2.17) * mm});
            skLineSegment(sketch, "E286", {"start": v(35.54, -2.17) * mm, "end": v(36, -1.99) * mm});
            skSolve(sketch);
        }
        {
            var Q0;
            Q0=makeQuery(id+"F0.imprint","IMPRINT",FACE,{"disambiguationData":[TD([[makeQuery(id+"F0.imprint","IMPRINT",EDGE,{"derivedFrom":sQuery(id+"F0.wireOp",EDGE,"E0")}),1.0]])]});
            extrude(context, id + "F1", {"entities" : qUnion([Q0]), "depth" : 6.35 * mm, "offsetDistance" : 25.4 * mm});
        }
        {
            var Q0;
            Q0=makeQuery(id+"F1.opExtrude","CAP_FACE",FACE,{"disambiguationData":[OSD([sQuery(id+"F0.wireOp",EDGE,"E0"),sQuery(id+"F0.wireOp",EDGE,"E1"),sQuery(id+"F0.wireOp",EDGE,"E2"),sQuery(id+"F0.wireOp",EDGE,"E3"),sQuery(id+"F0.wireOp",EDGE,"E4"),sQuery(id+"F0.wireOp",EDGE,"E5"),sQuery(id+"F0.wireOp",EDGE,"E6"),sQuery(id+"F0.wireOp",EDGE,"E7"),sQuery(id+"F0.wireOp",EDGE,"E8"),sQuery(id+"F0.wireOp",EDGE,"E9"),sQuery(id+"F0.wireOp",EDGE,"E10"),sQuery(id+"F0.wireOp",EDGE,"E11"),sQuery(id+"F0.wireOp",EDGE,"E12"),sQuery(id+"F0.wireOp",EDGE,"E13"),sQuery(id+"F0.wireOp",EDGE,"E14"),sQuery(id+"F0.wireOp",EDGE,"E15"),sQuery(id+"F0.wireOp",EDGE,"E16"),sQuery(id+"F0.wireOp",EDGE,"E17"),sQuery(id+"F0.wireOp",EDGE,"E18"),sQuery(id+"F0.wireOp",EDGE,"E19"),sQuery(id+"F0.wireOp",EDGE,"E20"),sQuery(id+"F0.wireOp",EDGE,"E21"),sQuery(id+"F0.wireOp",EDGE,"E22"),sQuery(id+"F0.wireOp",EDGE,"E23"),sQuery(id+"F0.wireOp",EDGE,"E24"),sQuery(id+"F0.wireOp",EDGE,"E25"),sQuery(id+"F0.wireOp",EDGE,"E26"),sQuery(id+"F0.wireOp",EDGE,"E27"),sQuery(id+"F0.wireOp",EDGE,"E28"),sQuery(id+"F0.wireOp",EDGE,"E29"),sQuery(id+"F0.wireOp",EDGE,"E30"),sQuery(id+"F0.wireOp",EDGE,"E31"),sQuery(id+"F0.wireOp",EDGE,"E32"),sQuery(id+"F0.wireOp",EDGE,"E33"),sQuery(id+"F0.wireOp",EDGE,"E34"),sQuery(id+"F0.wireOp",EDGE,"E35"),sQuery(id+"F0.wireOp",EDGE,"E36"),sQuery(id+"F0.wireOp",EDGE,"E37"),sQuery(id+"F0.wireOp",EDGE,"E38"),sQuery(id+"F0.wireOp",EDGE,"E39"),sQuery(id+"F0.wireOp",EDGE,"E40"),sQuery(id+"F0.wireOp",EDGE,"E41"),sQuery(id+"F0.wireOp",EDGE,"E42"),sQuery(id+"F0.wireOp",EDGE,"E43"),sQuery(id+"F0.wireOp",EDGE,"E44"),sQuery(id+"F0.wireOp",EDGE,"E45"),sQuery(id+"F0.wireOp",EDGE,"E46"),sQuery(id+"F0.wireOp",EDGE,"E47"),sQuery(id+"F0.wireOp",EDGE,"E48"),sQuery(id+"F0.wireOp",EDGE,"E49"),sQuery(id+"F0.wireOp",EDGE,"E50"),sQuery(id+"F0.wireOp",EDGE,"E51"),sQuery(id+"F0.wireOp",EDGE,"E52"),sQuery(id+"F0.wireOp",EDGE,"E53"),sQuery(id+"F0.wireOp",EDGE,"E54"),sQuery(id+"F0.wireOp",EDGE,"E55"),sQuery(id+"F0.wireOp",EDGE,"E56"),sQuery(id+"F0.wireOp",EDGE,"E57"),sQuery(id+"F0.wireOp",EDGE,"E58"),sQuery(id+"F0.wireOp",EDGE,"E59"),sQuery(id+"F0.wireOp",EDGE,"E60"),sQuery(id+"F0.wireOp",EDGE,"E61"),sQuery(id+"F0.wireOp",EDGE,"E62"),sQuery(id+"F0.wireOp",EDGE,"E63"),sQuery(id+"F0.wireOp",EDGE,"E64"),sQuery(id+"F0.wireOp",EDGE,"E65"),sQuery(id+"F0.wireOp",EDGE,"E66"),sQuery(id+"F0.wireOp",EDGE,"E67"),sQuery(id+"F0.wireOp",EDGE,"E68"),sQuery(id+"F0.wireOp",EDGE,"E69"),sQuery(id+"F0.wireOp",EDGE,"E70"),sQuery(id+"F0.wireOp",EDGE,"E71"),sQuery(id+"F0.wireOp",EDGE,"E72"),sQuery(id+"F0.wireOp",EDGE,"E73"),sQuery(id+"F0.wireOp",EDGE,"E74"),sQuery(id+"F0.wireOp",EDGE,"E75"),sQuery(id+"F0.wireOp",EDGE,"E76"),sQuery(id+"F0.wireOp",EDGE,"E77"),sQuery(id+"F0.wireOp",EDGE,"E78"),sQuery(id+"F0.wireOp",EDGE,"E79"),sQuery(id+"F0.wireOp",EDGE,"E80"),sQuery(id+"F0.wireOp",EDGE,"E81"),sQuery(id+"F0.wireOp",EDGE,"E82"),sQuery(id+"F0.wireOp",EDGE,"E83"),sQuery(id+"F0.wireOp",EDGE,"E84"),sQuery(id+"F0.wireOp",EDGE,"E85"),sQuery(id+"F0.wireOp",EDGE,"E86"),sQuery(id+"F0.wireOp",EDGE,"E87"),sQuery(id+"F0.wireOp",EDGE,"E88"),sQuery(id+"F0.wireOp",EDGE,"E89"),sQuery(id+"F0.wireOp",EDGE,"E90"),sQuery(id+"F0.wireOp",EDGE,"E91"),sQuery(id+"F0.wireOp",EDGE,"E92"),sQuery(id+"F0.wireOp",EDGE,"E93"),sQuery(id+"F0.wireOp",EDGE,"E94"),sQuery(id+"F0.wireOp",EDGE,"E95"),sQuery(id+"F0.wireOp",EDGE,"E96"),sQuery(id+"F0.wireOp",EDGE,"E97"),sQuery(id+"F0.wireOp",EDGE,"E98"),sQuery(id+"F0.wireOp",EDGE,"E99"),sQuery(id+"F0.wireOp",EDGE,"E100"),sQuery(id+"F0.wireOp",EDGE,"E101"),sQuery(id+"F0.wireOp",EDGE,"E102"),sQuery(id+"F0.wireOp",EDGE,"E103"),sQuery(id+"F0.wireOp",EDGE,"E104"),sQuery(id+"F0.wireOp",EDGE,"E105"),sQuery(id+"F0.wireOp",EDGE,"E106"),sQuery(id+"F0.wireOp",EDGE,"E107"),sQuery(id+"F0.wireOp",EDGE,"E108"),sQuery(id+"F0.wireOp",EDGE,"E109"),sQuery(id+"F0.wireOp",EDGE,"E110"),sQuery(id+"F0.wireOp",EDGE,"E111"),sQuery(id+"F0.wireOp",EDGE,"E112"),sQuery(id+"F0.wireOp",EDGE,"E113"),sQuery(id+"F0.wireOp",EDGE,"E114"),sQuery(id+"F0.wireOp",EDGE,"E115"),sQuery(id+"F0.wireOp",EDGE,"E116"),sQuery(id+"F0.wireOp",EDGE,"E117"),sQuery(id+"F0.wireOp",EDGE,"E118"),sQuery(id+"F0.wireOp",EDGE,"E119"),sQuery(id+"F0.wireOp",EDGE,"E120"),sQuery(id+"F0.wireOp",EDGE,"E121"),sQuery(id+"F0.wireOp",EDGE,"E122"),sQuery(id+"F0.wireOp",EDGE,"E123"),sQuery(id+"F0.wireOp",EDGE,"E124"),sQuery(id+"F0.wireOp",EDGE,"E125"),sQuery(id+"F0.wireOp",EDGE,"E126"),sQuery(id+"F0.wireOp",EDGE,"E127"),sQuery(id+"F0.wireOp",EDGE,"E128"),sQuery(id+"F0.wireOp",EDGE,"E129"),sQuery(id+"F0.wireOp",EDGE,"E130"),sQuery(id+"F0.wireOp",EDGE,"E131"),sQuery(id+"F0.wireOp",EDGE,"E132"),sQuery(id+"F0.wireOp",EDGE,"E133"),sQuery(id+"F0.wireOp",EDGE,"E134"),sQuery(id+"F0.wireOp",EDGE,"E135"),sQuery(id+"F0.wireOp",EDGE,"E136"),sQuery(id+"F0.wireOp",EDGE,"E137"),sQuery(id+"F0.wireOp",EDGE,"E138"),sQuery(id+"F0.wireOp",EDGE,"E139"),sQuery(id+"F0.wireOp",EDGE,"E140"),sQuery(id+"F0.wireOp",EDGE,"E141"),sQuery(id+"F0.wireOp",EDGE,"E142"),sQuery(id+"F0.wireOp",EDGE,"E143"),sQuery(id+"F0.wireOp",EDGE,"E144"),sQuery(id+"F0.wireOp",EDGE,"E145"),sQuery(id+"F0.wireOp",EDGE,"E146"),sQuery(id+"F0.wireOp",EDGE,"E147"),sQuery(id+"F0.wireOp",EDGE,"E148"),sQuery(id+"F0.wireOp",EDGE,"E149"),sQuery(id+"F0.wireOp",EDGE,"E150"),sQuery(id+"F0.wireOp",EDGE,"E151"),sQuery(id+"F0.wireOp",EDGE,"E152"),sQuery(id+"F0.wireOp",EDGE,"E153"),sQuery(id+"F0.wireOp",EDGE,"E154"),sQuery(id+"F0.wireOp",EDGE,"E155"),sQuery(id+"F0.wireOp",EDGE,"E156"),sQuery(id+"F0.wireOp",EDGE,"E157"),sQuery(id+"F0.wireOp",EDGE,"E158"),sQuery(id+"F0.wireOp",EDGE,"E159"),sQuery(id+"F0.wireOp",EDGE,"E160"),sQuery(id+"F0.wireOp",EDGE,"E161"),sQuery(id+"F0.wireOp",EDGE,"E162"),sQuery(id+"F0.wireOp",EDGE,"E163"),sQuery(id+"F0.wireOp",EDGE,"E164"),sQuery(id+"F0.wireOp",EDGE,"E165"),sQuery(id+"F0.wireOp",EDGE,"E166"),sQuery(id+"F0.wireOp",EDGE,"E167"),sQuery(id+"F0.wireOp",EDGE,"E168"),sQuery(id+"F0.wireOp",EDGE,"E169"),sQuery(id+"F0.wireOp",EDGE,"E170"),sQuery(id+"F0.wireOp",EDGE,"E171"),sQuery(id+"F0.wireOp",EDGE,"E172"),sQuery(id+"F0.wireOp",EDGE,"E173"),sQuery(id+"F0.wireOp",EDGE,"E174"),sQuery(id+"F0.wireOp",EDGE,"E175"),sQuery(id+"F0.wireOp",EDGE,"E176"),sQuery(id+"F0.wireOp",EDGE,"E177"),sQuery(id+"F0.wireOp",EDGE,"E178"),sQuery(id+"F0.wireOp",EDGE,"E179"),sQuery(id+"F0.wireOp",EDGE,"E180"),sQuery(id+"F0.wireOp",EDGE,"E181"),sQuery(id+"F0.wireOp",EDGE,"E182"),sQuery(id+"F0.wireOp",EDGE,"E183"),sQuery(id+"F0.wireOp",EDGE,"E184"),sQuery(id+"F0.wireOp",EDGE,"E185"),sQuery(id+"F0.wireOp",EDGE,"E186"),sQuery(id+"F0.wireOp",EDGE,"E187"),sQuery(id+"F0.wireOp",EDGE,"E188"),sQuery(id+"F0.wireOp",EDGE,"E189"),sQuery(id+"F0.wireOp",EDGE,"E190"),sQuery(id+"F0.wireOp",EDGE,"E191"),sQuery(id+"F0.wireOp",EDGE,"E192"),sQuery(id+"F0.wireOp",EDGE,"E193"),sQuery(id+"F0.wireOp",EDGE,"E194"),sQuery(id+"F0.wireOp",EDGE,"E195"),sQuery(id+"F0.wireOp",EDGE,"E196"),sQuery(id+"F0.wireOp",EDGE,"E197"),sQuery(id+"F0.wireOp",EDGE,"E198"),sQuery(id+"F0.wireOp",EDGE,"E199"),sQuery(id+"F0.wireOp",EDGE,"E200"),sQuery(id+"F0.wireOp",EDGE,"E201"),sQuery(id+"F0.wireOp",EDGE,"E202"),sQuery(id+"F0.wireOp",EDGE,"E203"),sQuery(id+"F0.wireOp",EDGE,"E204"),sQuery(id+"F0.wireOp",EDGE,"E205"),sQuery(id+"F0.wireOp",EDGE,"E206"),sQuery(id+"F0.wireOp",EDGE,"E207"),sQuery(id+"F0.wireOp",EDGE,"E208"),sQuery(id+"F0.wireOp",EDGE,"E209"),sQuery(id+"F0.wireOp",EDGE,"E210"),sQuery(id+"F0.wireOp",EDGE,"E211"),sQuery(id+"F0.wireOp",EDGE,"E212"),sQuery(id+"F0.wireOp",EDGE,"E213"),sQuery(id+"F0.wireOp",EDGE,"E214"),sQuery(id+"F0.wireOp",EDGE,"E215"),sQuery(id+"F0.wireOp",EDGE,"E216"),sQuery(id+"F0.wireOp",EDGE,"E217"),sQuery(id+"F0.wireOp",EDGE,"E218"),sQuery(id+"F0.wireOp",EDGE,"E219"),sQuery(id+"F0.wireOp",EDGE,"E220"),sQuery(id+"F0.wireOp",EDGE,"E221"),sQuery(id+"F0.wireOp",EDGE,"E222"),sQuery(id+"F0.wireOp",EDGE,"E223"),sQuery(id+"F0.wireOp",EDGE,"E224"),sQuery(id+"F0.wireOp",EDGE,"E225"),sQuery(id+"F0.wireOp",EDGE,"E226"),sQuery(id+"F0.wireOp",EDGE,"E227"),sQuery(id+"F0.wireOp",EDGE,"E228"),sQuery(id+"F0.wireOp",EDGE,"E229"),sQuery(id+"F0.wireOp",EDGE,"E230"),sQuery(id+"F0.wireOp",EDGE,"E231"),sQuery(id+"F0.wireOp",EDGE,"E232"),sQuery(id+"F0.wireOp",EDGE,"E233"),sQuery(id+"F0.wireOp",EDGE,"E234"),sQuery(id+"F0.wireOp",EDGE,"E235"),sQuery(id+"F0.wireOp",EDGE,"E236"),sQuery(id+"F0.wireOp",EDGE,"E237"),sQuery(id+"F0.wireOp",EDGE,"E238"),sQuery(id+"F0.wireOp",EDGE,"E239"),sQuery(id+"F0.wireOp",EDGE,"E240"),sQuery(id+"F0.wireOp",EDGE,"E241"),sQuery(id+"F0.wireOp",EDGE,"E242"),sQuery(id+"F0.wireOp",EDGE,"E243"),sQuery(id+"F0.wireOp",EDGE,"E244"),sQuery(id+"F0.wireOp",EDGE,"E245"),sQuery(id+"F0.wireOp",EDGE,"E246"),sQuery(id+"F0.wireOp",EDGE,"E247"),sQuery(id+"F0.wireOp",EDGE,"E248"),sQuery(id+"F0.wireOp",EDGE,"E249"),sQuery(id+"F0.wireOp",EDGE,"E250"),sQuery(id+"F0.wireOp",EDGE,"E251"),sQuery(id+"F0.wireOp",EDGE,"E252"),sQuery(id+"F0.wireOp",EDGE,"E253"),sQuery(id+"F0.wireOp",EDGE,"E254"),sQuery(id+"F0.wireOp",EDGE,"E255"),sQuery(id+"F0.wireOp",EDGE,"E256"),sQuery(id+"F0.wireOp",EDGE,"E257"),sQuery(id+"F0.wireOp",EDGE,"E258"),sQuery(id+"F0.wireOp",EDGE,"E259"),sQuery(id+"F0.wireOp",EDGE,"E260"),sQuery(id+"F0.wireOp",EDGE,"E261"),sQuery(id+"F0.wireOp",EDGE,"E262"),sQuery(id+"F0.wireOp",EDGE,"E263"),sQuery(id+"F0.wireOp",EDGE,"E264"),sQuery(id+"F0.wireOp",EDGE,"E265"),sQuery(id+"F0.wireOp",EDGE,"E266"),sQuery(id+"F0.wireOp",EDGE,"E267"),sQuery(id+"F0.wireOp",EDGE,"E268"),sQuery(id+"F0.wireOp",EDGE,"E269"),sQuery(id+"F0.wireOp",EDGE,"E270"),sQuery(id+"F0.wireOp",EDGE,"E271"),sQuery(id+"F0.wireOp",EDGE,"E272"),sQuery(id+"F0.wireOp",EDGE,"E273"),sQuery(id+"F0.wireOp",EDGE,"E274"),sQuery(id+"F0.wireOp",EDGE,"E275"),sQuery(id+"F0.wireOp",EDGE,"E276"),sQuery(id+"F0.wireOp",EDGE,"E277"),sQuery(id+"F0.wireOp",EDGE,"E278"),sQuery(id+"F0.wireOp",EDGE,"E279"),sQuery(id+"F0.wireOp",EDGE,"E280"),sQuery(id+"F0.wireOp",EDGE,"E281"),sQuery(id+"F0.wireOp",EDGE,"E282"),sQuery(id+"F0.wireOp",EDGE,"E283"),sQuery(id+"F0.wireOp",EDGE,"E284"),sQuery(id+"F0.wireOp",EDGE,"E285"),sQuery(id+"F0.wireOp",EDGE,"E286")])],"isStart":false});
            var sketch = newSketch(context, id + "F2", { "sketchPlane" : qUnion([Q0])});
            skText(sketch, "E287", { "text": "R", "fontName": "NotoSerif-Bold.ttf"});
            skText(sketch, "E288", { "text": "M", "fontName": "NotoSerif-Bold.ttf"});
            skText(sketch, "E289", { "text": "M", "fontName": "NotoSerif-Bold.ttf"});
            skText(sketch, "E290", { "text": "G", "fontName": "NotoSerif-Bold.ttf"});
            const initialGuessF2  = {"E287": [-0.01138, -0.00651, 0.42262, 0.9063, 0.018], "E288": [0.00837, -0.00836, 0.42262, 0.9063, 0.008], "E289": [-0.00127, -0.00833, 0.42262, 0.9063, 0.008], "E290": [0.01913, -0.00663, 0.42262, 0.9063, 0.008]};
            skSetInitialGuess(sketch, initialGuessF2);
            skSolve(sketch);
        }
        {
            var Q0;
            Q0=qSketchRegion(id+"F2",true);
            extrude(context, id + "F3", {"entities" : qUnion([Q0]), "operationType" : NewBodyOperationType.REMOVE, "oppositeDirection" : true, "depth" : (6.35 / 2) * mm, "offsetDistance" : 25 * mm});
        }
    });
